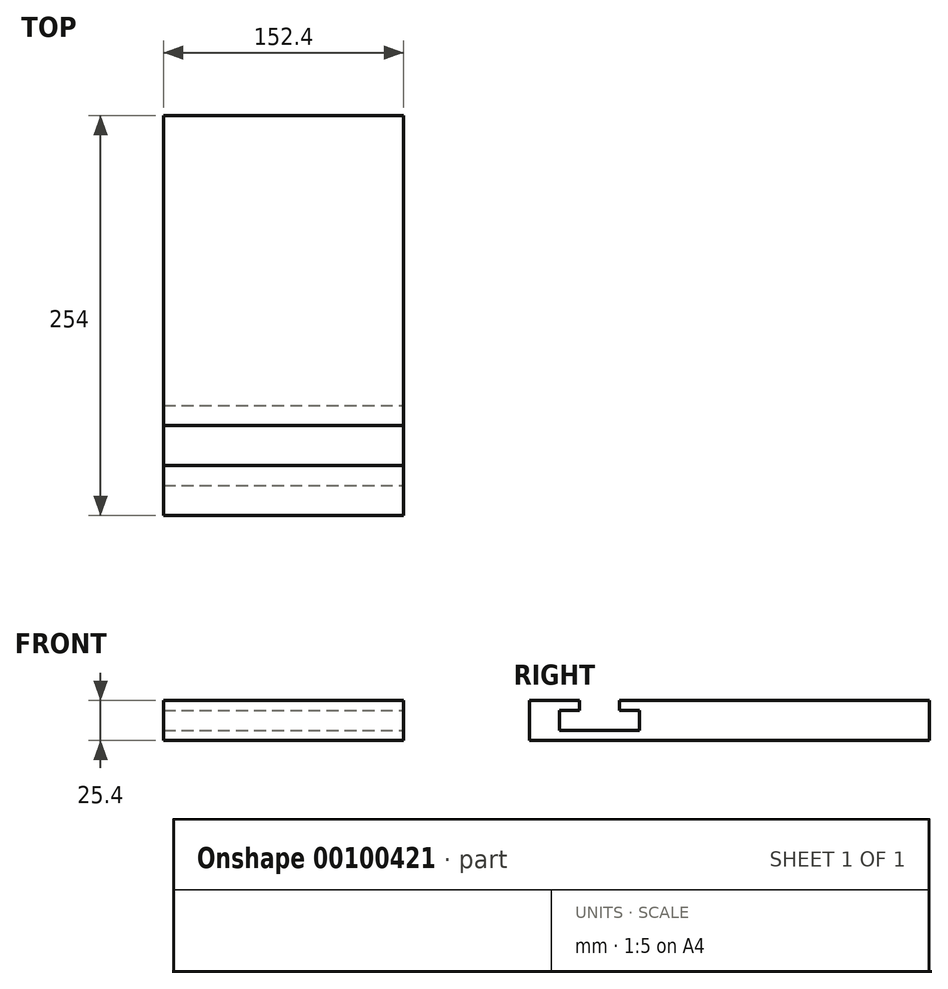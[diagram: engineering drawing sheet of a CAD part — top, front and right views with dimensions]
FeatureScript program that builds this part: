
annotation { "Feature Type Name" : "Feature", "Feature Type Description" : "" }
export const myFeature = defineFeature(function(context is Context, id is Id, definition is map)
    precondition{}
    {
        {
            var Q0;
            Q0=qCreatedBy(makeId("Top.planeOp"),FACE);
            var sketch = newSketch(context, id + "F0", { "sketchPlane" : qUnion([Q0])});
            skLineSegment(sketch, "E0.bottom", {"start": v(0, 0) * mm, "end": v(152.4, 0) * mm});
            skLineSegment(sketch, "E0.top", {"start": v(0, 254) * mm, "end": v(152.4, 254) * mm});
            skLineSegment(sketch, "E0.left", {"start": v(0, 0) * mm, "end": v(0, 254) * mm});
            skLineSegment(sketch, "E0.right", {"start": v(152.4, 0) * mm, "end": v(152.4, 254) * mm});
            skPoint(sketch, "E1.firstSnap0", {"position": v(76.2, 254) * mm});
            skSolve(sketch);
        }
        {
            var Q0;
            Q0 = qSketchRegion(id + "F0", true);
            extrude(context, id + "F1", {"entities" : qUnion([Q0]), "oppositeDirection" : true, "depth" : 25.4 * mm});
        }
        {
            var Q0;
            Q0=makeQuery(id+"F1.opExtrude","SWEPT_FACE",FACE,{"disambiguationData":[OSD([sQuery(id+"F0.wireOp",EDGE,"E0.right")])]});
            var sketch = newSketch(context, id + "F2", { "sketchPlane" : qUnion([Q0])});
            skLineSegment(sketch, "E2", {"start": v(57.15, 0) * mm, "end": v(31.75, 0) * mm});
            skLineSegment(sketch, "E3", {"start": v(31.75, 0) * mm, "end": v(31.75, -6.35) * mm});
            skLineSegment(sketch, "E4", {"start": v(31.75, -6.35) * mm, "end": v(19.05, -6.35) * mm});
            skPoint(sketch, "E5.orphan", {"position": v(19.05, 0) * mm});
            skLineSegment(sketch, "E6", {"start": v(19.05, -6.35) * mm, "end": v(19.05, -19.05) * mm});
            skLineSegment(sketch, "E7", {"start": v(57.15, 0) * mm, "end": v(57.15, -6.35) * mm});
            skLineSegment(sketch, "E8", {"start": v(57.15, -6.35) * mm, "end": v(69.85, -6.35) * mm});
            skLineSegment(sketch, "E9", {"start": v(69.85, -6.35) * mm, "end": v(69.85, -19.05) * mm});
            skLineSegment(sketch, "E10", {"start": v(19.05, -19.05) * mm, "end": v(69.85, -19.05) * mm});
            skSolve(sketch);
        }
        {
            var Q0;
            Q0 = qSketchRegion(id + "F2", true);
            extrude(context, id + "F3", {"entities" : qUnion([Q0]), "operationType" : NewBodyOperationType.REMOVE, "endBound" : BoundingType.THROUGH_ALL, "oppositeDirection" : true, "depth" : 25.4 * mm});
        }
    });
